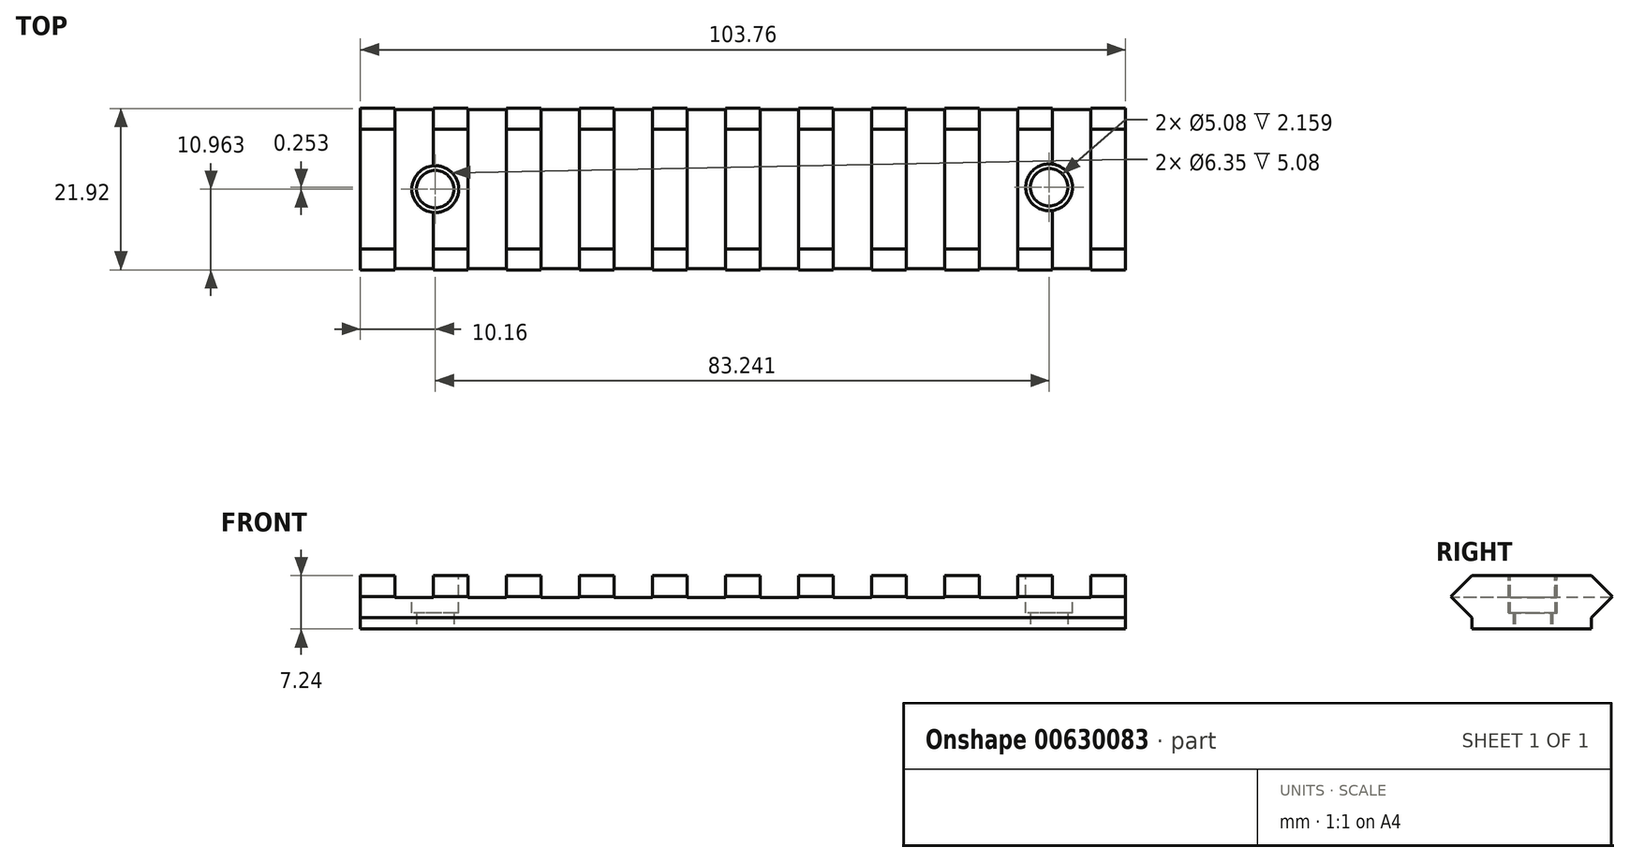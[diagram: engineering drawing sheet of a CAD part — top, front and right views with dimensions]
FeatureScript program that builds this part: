
annotation { "Feature Type Name" : "Feature", "Feature Type Description" : "" }
export const myFeature = defineFeature(function(context is Context, id is Id, definition is map)
    precondition{}
    {
        {
            var Q0;
            Q0=qCreatedBy(makeId("Right.planeOp"),FACE);
            var sketch = newSketch(context, id + "F0", { "sketchPlane" : qUnion([Q0])});
            skLineSegment(sketch, "E0", {"start": v(0, 0) * mm, "end": v(0, 1.52) * mm});
            skLineSegment(sketch, "E1", {"start": v(0, 1.52) * mm, "end": v(-2.86, 4.38) * mm});
            skLineSegment(sketch, "E2", {"start": v(-2.86, 4.38) * mm, "end": v(0, 7.24) * mm});
            skLineSegment(sketch, "E3", {"start": v(0, 7.24) * mm, "end": v(16.2, 7.24) * mm});
            skLineSegment(sketch, "E4", {"start": v(0, 0) * mm, "end": v(16.2, 0) * mm});
            skLineSegment(sketch, "E5", {"start": v(16.2, 0) * mm, "end": v(16.2, 1.52) * mm});
            skLineSegment(sketch, "E6", {"start": v(16.2, 1.52) * mm, "end": v(19.06, 4.38) * mm});
            skLineSegment(sketch, "E7", {"start": v(19.06, 4.38) * mm, "end": v(16.2, 7.24) * mm});
            skSolve(sketch);
        }
        {
            var Q0;
            Q0=makeQuery(id+"F0.imprint","IMPRINT",FACE,{"disambiguationData":[TD([[makeQuery(id+"F0.imprint","IMPRINT",EDGE,{"derivedFrom":sQuery(id+"F0.wireOp",EDGE,"E0")}),-1.0]])]});
            extrude(context, id + "F1", {"entities" : qUnion([Q0]), "depth" : 103.76 * mm});
        }
        {
            var Q0;
            Q0=makeQuery(id+"F1.opExtrude","SWEPT_FACE",FACE,{"disambiguationData":[OSD([sQuery(id+"F0.wireOp",EDGE,"E3")])]});
            var sketch = newSketch(context, id + "F2", { "sketchPlane" : qUnion([Q0])});
            skLineSegment(sketch, "E8", {"start": v(0, 8.1) * mm, "end": v(4.7, 8.1) * mm, "construction": true});
            skLineSegment(sketch, "E9", {"start": v(4.7, 8.1) * mm, "end": v(4.7, 19.06) * mm});
            skLineSegment(sketch, "E10", {"start": v(4.7, 8.1) * mm, "end": v(4.7, -2.86) * mm});
            skLineSegment(sketch, "E11", {"start": v(4.7, 8.1) * mm, "end": v(9.9, 8.1) * mm, "construction": true});
            skLineSegment(sketch, "E12", {"start": v(4.7, 19.06) * mm, "end": v(9.9, 19.06) * mm});
            skLineSegment(sketch, "E13", {"start": v(9.9, 19.06) * mm, "end": v(9.9, -2.86) * mm});
            skLineSegment(sketch, "E14", {"start": v(4.7, -2.86) * mm, "end": v(9.9, -2.86) * mm});
            skLineSegment(sketch, "E15", {"start": v(9.9, 8.1) * mm, "end": v(14.6, 8.1) * mm, "construction": true});
            skLineSegment(sketch, "E16.bottom", {"start": v(14.6, 19.06) * mm, "end": v(19.81, 19.06) * mm});
            skLineSegment(sketch, "E16.top", {"start": v(14.6, -2.86) * mm, "end": v(19.81, -2.86) * mm});
            skLineSegment(sketch, "E16.left", {"start": v(14.6, 19.06) * mm, "end": v(14.6, -2.86) * mm});
            skLineSegment(sketch, "E16.right", {"start": v(19.81, 19.06) * mm, "end": v(19.81, -2.86) * mm});
            skLineSegment(sketch, "E17", {"start": v(19.81, 8.1) * mm, "end": v(24.51, 8.1) * mm, "construction": true});
            skLineSegment(sketch, "E18.bottom", {"start": v(24.51, 19.06) * mm, "end": v(29.72, 19.06) * mm});
            skLineSegment(sketch, "E18.top", {"start": v(24.51, -2.86) * mm, "end": v(29.72, -2.86) * mm});
            skLineSegment(sketch, "E18.left", {"start": v(24.51, 19.06) * mm, "end": v(24.51, -2.86) * mm});
            skLineSegment(sketch, "E18.right", {"start": v(29.72, 19.06) * mm, "end": v(29.72, -2.86) * mm});
            skLineSegment(sketch, "E19.bottom", {"start": v(34.42, 19.06) * mm, "end": v(39.62, 19.06) * mm});
            skLineSegment(sketch, "E19.top", {"start": v(34.42, -2.86) * mm, "end": v(39.62, -2.86) * mm});
            skLineSegment(sketch, "E19.left", {"start": v(34.42, 19.06) * mm, "end": v(34.42, -2.86) * mm});
            skLineSegment(sketch, "E19.right", {"start": v(39.62, 19.06) * mm, "end": v(39.62, -2.86) * mm});
            skLineSegment(sketch, "E20", {"start": v(39.62, 8.1) * mm, "end": v(44.32, 8.1) * mm, "construction": true});
            skLineSegment(sketch, "E21.bottom", {"start": v(44.32, 19.06) * mm, "end": v(49.53, 19.06) * mm});
            skLineSegment(sketch, "E21.top", {"start": v(44.32, -2.86) * mm, "end": v(49.53, -2.86) * mm});
            skLineSegment(sketch, "E21.left", {"start": v(44.32, 19.06) * mm, "end": v(44.32, -2.86) * mm});
            skLineSegment(sketch, "E21.right", {"start": v(49.53, 19.06) * mm, "end": v(49.53, -2.86) * mm});
            skLineSegment(sketch, "E22", {"start": v(49.53, 8.1) * mm, "end": v(54.23, 8.1) * mm, "construction": true});
            skLineSegment(sketch, "E23.bottom", {"start": v(54.23, 19.06) * mm, "end": v(59.44, 19.06) * mm});
            skLineSegment(sketch, "E23.top", {"start": v(54.23, -2.86) * mm, "end": v(59.44, -2.86) * mm});
            skLineSegment(sketch, "E23.left", {"start": v(54.23, 19.06) * mm, "end": v(54.23, -2.86) * mm});
            skLineSegment(sketch, "E23.right", {"start": v(59.44, 19.06) * mm, "end": v(59.44, -2.86) * mm});
            skLineSegment(sketch, "E24", {"start": v(59.44, 8.1) * mm, "end": v(64.13, 8.1) * mm, "construction": true});
            skLineSegment(sketch, "E25.bottom", {"start": v(64.13, 19.06) * mm, "end": v(69.34, 19.06) * mm});
            skLineSegment(sketch, "E25.top", {"start": v(64.13, -2.86) * mm, "end": v(69.34, -2.86) * mm});
            skLineSegment(sketch, "E25.left", {"start": v(64.13, 19.06) * mm, "end": v(64.13, -2.86) * mm});
            skLineSegment(sketch, "E25.right", {"start": v(69.34, 19.06) * mm, "end": v(69.34, -2.86) * mm});
            skLineSegment(sketch, "E26", {"start": v(69.34, 8.1) * mm, "end": v(74.04, 8.1) * mm, "construction": true});
            skLineSegment(sketch, "E27", {"start": v(29.72, 8.1) * mm, "end": v(34.42, 8.1) * mm, "construction": true});
            skLineSegment(sketch, "E28.bottom", {"start": v(74.04, 19.06) * mm, "end": v(79.25, 19.06) * mm});
            skLineSegment(sketch, "E28.top", {"start": v(74.04, -2.86) * mm, "end": v(79.25, -2.86) * mm});
            skLineSegment(sketch, "E28.left", {"start": v(74.04, 19.06) * mm, "end": v(74.04, -2.86) * mm});
            skLineSegment(sketch, "E28.right", {"start": v(79.25, 19.06) * mm, "end": v(79.25, -2.86) * mm});
            skLineSegment(sketch, "E29", {"start": v(79.25, 8.1) * mm, "end": v(83.95, 8.1) * mm, "construction": true});
            skLineSegment(sketch, "E30.bottom", {"start": v(83.95, 19.06) * mm, "end": v(89.15, 19.06) * mm});
            skLineSegment(sketch, "E30.top", {"start": v(83.95, -2.86) * mm, "end": v(89.15, -2.86) * mm});
            skLineSegment(sketch, "E30.left", {"start": v(83.95, 19.06) * mm, "end": v(83.95, -2.86) * mm});
            skLineSegment(sketch, "E30.right", {"start": v(89.15, 19.06) * mm, "end": v(89.15, -2.86) * mm});
            skLineSegment(sketch, "E31", {"start": v(89.15, 8.1) * mm, "end": v(93.85, 8.1) * mm, "construction": true});
            skLineSegment(sketch, "E32.bottom", {"start": v(93.85, 19.15) * mm, "end": v(99.06, 19.15) * mm});
            skLineSegment(sketch, "E32.top", {"start": v(93.85, -2.94) * mm, "end": v(99.06, -2.94) * mm});
            skLineSegment(sketch, "E32.left", {"start": v(93.85, 19.15) * mm, "end": v(93.85, -2.94) * mm});
            skLineSegment(sketch, "E32.right", {"start": v(99.06, 19.15) * mm, "end": v(99.06, -2.94) * mm});
            skSolve(sketch);
        }
        {
            var Q0;
            {var subQ0=sQuery(id+"F2.wireOp",EDGE,"E14");Q0=makeQuery(id+"F2.imprint","IMPRINT",FACE,{"disambiguationData":[TD([[makeQuery(id+"F2.imprint","IMPRINT",EDGE,{"derivedFrom":subQ0}),1.0]])]});}
            var Q1;
            {var subQ0=sQuery(id+"F2.wireOp",EDGE,"E10");var subQ8=sQuery(id+"F2.wireOp",EDGE,"E9");var subQ9=makeQuery(id+"F2.imprint","INTERSECT",VERTEX,{"derivedFrom":[subQ8,subQ0]});Q1=makeQuery(id+"F2.imprint","IMPRINT",FACE,{"disambiguationData":[TD([[makeQuery(id+"F2.imprint","IMPRINT",EDGE,{"disambiguationData":[TD([[subQ9,-1.0]])],"derivedFrom":subQ8}),-1.0]])]});}
            var Q2;
            {var subQ0=sQuery(id+"F2.wireOp",EDGE,"E12");Q2=makeQuery(id+"F2.imprint","IMPRINT",FACE,{"disambiguationData":[TD([[makeQuery(id+"F2.imprint","IMPRINT",EDGE,{"derivedFrom":subQ0}),-1.0]])]});}
            var Q3;
            {var subQ0=sQuery(id+"F2.wireOp",EDGE,"E16.bottom");Q3=makeQuery(id+"F2.imprint","IMPRINT",FACE,{"disambiguationData":[TD([[makeQuery(id+"F2.imprint","IMPRINT",EDGE,{"derivedFrom":subQ0}),-1.0]])]});}
            var Q4;
            {var subQ0=sQuery(id+"F2.wireOp",EDGE,"E16.left");var subQ1=sQuery(id+"F0.wireOp",EDGE,"E3");var subQ2=makeQuery(id+"F1.opExtrude","SWEPT_EDGE",EDGE,{"disambiguationData":[OSD([subQ1,sQuery(id+"F0.wireOp",EDGE,"E7")])]});var subQ3=makeQuery(id+"F2.imprint","INTERSECT",VERTEX,{"derivedFrom":[subQ2,subQ0]});Q4=makeQuery(id+"F2.imprint","IMPRINT",FACE,{"disambiguationData":[TD([[makeQuery(id+"F2.imprint","IMPRINT",EDGE,{"disambiguationData":[TD([[subQ3,-1.0]])],"derivedFrom":subQ0}),1.0]])]});}
            var Q5;
            {var subQ0=sQuery(id+"F2.wireOp",EDGE,"E16.top");Q5=makeQuery(id+"F2.imprint","IMPRINT",FACE,{"disambiguationData":[TD([[makeQuery(id+"F2.imprint","IMPRINT",EDGE,{"derivedFrom":subQ0}),1.0]])]});}
            var Q6;
            {var subQ0=sQuery(id+"F2.wireOp",EDGE,"E18.bottom");Q6=makeQuery(id+"F2.imprint","IMPRINT",FACE,{"disambiguationData":[TD([[makeQuery(id+"F2.imprint","IMPRINT",EDGE,{"derivedFrom":subQ0}),-1.0]])]});}
            var Q7;
            {var subQ0=sQuery(id+"F2.wireOp",EDGE,"E18.left");var subQ1=sQuery(id+"F0.wireOp",EDGE,"E3");var subQ2=makeQuery(id+"F1.opExtrude","SWEPT_EDGE",EDGE,{"disambiguationData":[OSD([subQ1,sQuery(id+"F0.wireOp",EDGE,"E7")])]});var subQ3=makeQuery(id+"F2.imprint","INTERSECT",VERTEX,{"derivedFrom":[subQ2,subQ0]});Q7=makeQuery(id+"F2.imprint","IMPRINT",FACE,{"disambiguationData":[TD([[makeQuery(id+"F2.imprint","IMPRINT",EDGE,{"disambiguationData":[TD([[subQ3,-1.0]])],"derivedFrom":subQ0}),1.0]])]});}
            var Q8;
            {var subQ0=sQuery(id+"F2.wireOp",EDGE,"E18.top");Q8=makeQuery(id+"F2.imprint","IMPRINT",FACE,{"disambiguationData":[TD([[makeQuery(id+"F2.imprint","IMPRINT",EDGE,{"derivedFrom":subQ0}),1.0]])]});}
            var Q9;
            {var subQ0=sQuery(id+"F2.wireOp",EDGE,"E19.bottom");Q9=makeQuery(id+"F2.imprint","IMPRINT",FACE,{"disambiguationData":[TD([[makeQuery(id+"F2.imprint","IMPRINT",EDGE,{"derivedFrom":subQ0}),-1.0]])]});}
            var Q10;
            {var subQ0=sQuery(id+"F2.wireOp",EDGE,"E19.left");var subQ1=sQuery(id+"F0.wireOp",EDGE,"E3");var subQ2=makeQuery(id+"F1.opExtrude","SWEPT_EDGE",EDGE,{"disambiguationData":[OSD([subQ1,sQuery(id+"F0.wireOp",EDGE,"E7")])]});var subQ3=makeQuery(id+"F2.imprint","INTERSECT",VERTEX,{"derivedFrom":[subQ2,subQ0]});Q10=makeQuery(id+"F2.imprint","IMPRINT",FACE,{"disambiguationData":[TD([[makeQuery(id+"F2.imprint","IMPRINT",EDGE,{"disambiguationData":[TD([[subQ3,-1.0]])],"derivedFrom":subQ0}),1.0]])]});}
            var Q11;
            {var subQ0=sQuery(id+"F2.wireOp",EDGE,"E19.top");Q11=makeQuery(id+"F2.imprint","IMPRINT",FACE,{"disambiguationData":[TD([[makeQuery(id+"F2.imprint","IMPRINT",EDGE,{"derivedFrom":subQ0}),1.0]])]});}
            var Q12;
            {var subQ0=sQuery(id+"F2.wireOp",EDGE,"E21.bottom");Q12=makeQuery(id+"F2.imprint","IMPRINT",FACE,{"disambiguationData":[TD([[makeQuery(id+"F2.imprint","IMPRINT",EDGE,{"derivedFrom":subQ0}),-1.0]])]});}
            var Q13;
            {var subQ0=sQuery(id+"F2.wireOp",EDGE,"E21.left");var subQ1=sQuery(id+"F0.wireOp",EDGE,"E3");var subQ2=makeQuery(id+"F1.opExtrude","SWEPT_EDGE",EDGE,{"disambiguationData":[OSD([subQ1,sQuery(id+"F0.wireOp",EDGE,"E7")])]});var subQ3=makeQuery(id+"F2.imprint","INTERSECT",VERTEX,{"derivedFrom":[subQ2,subQ0]});Q13=makeQuery(id+"F2.imprint","IMPRINT",FACE,{"disambiguationData":[TD([[makeQuery(id+"F2.imprint","IMPRINT",EDGE,{"disambiguationData":[TD([[subQ3,-1.0]])],"derivedFrom":subQ0}),1.0]])]});}
            var Q14;
            {var subQ0=sQuery(id+"F2.wireOp",EDGE,"E21.top");Q14=makeQuery(id+"F2.imprint","IMPRINT",FACE,{"disambiguationData":[TD([[makeQuery(id+"F2.imprint","IMPRINT",EDGE,{"derivedFrom":subQ0}),1.0]])]});}
            var Q15;
            {var subQ0=sQuery(id+"F2.wireOp",EDGE,"E23.bottom");Q15=makeQuery(id+"F2.imprint","IMPRINT",FACE,{"disambiguationData":[TD([[makeQuery(id+"F2.imprint","IMPRINT",EDGE,{"derivedFrom":subQ0}),-1.0]])]});}
            var Q16;
            {var subQ0=sQuery(id+"F2.wireOp",EDGE,"E23.left");var subQ1=sQuery(id+"F0.wireOp",EDGE,"E3");var subQ2=makeQuery(id+"F1.opExtrude","SWEPT_EDGE",EDGE,{"disambiguationData":[OSD([subQ1,sQuery(id+"F0.wireOp",EDGE,"E7")])]});var subQ3=makeQuery(id+"F2.imprint","INTERSECT",VERTEX,{"derivedFrom":[subQ2,subQ0]});Q16=makeQuery(id+"F2.imprint","IMPRINT",FACE,{"disambiguationData":[TD([[makeQuery(id+"F2.imprint","IMPRINT",EDGE,{"disambiguationData":[TD([[subQ3,-1.0]])],"derivedFrom":subQ0}),1.0]])]});}
            var Q17;
            {var subQ0=sQuery(id+"F2.wireOp",EDGE,"E23.top");Q17=makeQuery(id+"F2.imprint","IMPRINT",FACE,{"disambiguationData":[TD([[makeQuery(id+"F2.imprint","IMPRINT",EDGE,{"derivedFrom":subQ0}),1.0]])]});}
            var Q18;
            {var subQ0=sQuery(id+"F2.wireOp",EDGE,"E25.bottom");Q18=makeQuery(id+"F2.imprint","IMPRINT",FACE,{"disambiguationData":[TD([[makeQuery(id+"F2.imprint","IMPRINT",EDGE,{"derivedFrom":subQ0}),-1.0]])]});}
            var Q19;
            {var subQ0=sQuery(id+"F2.wireOp",EDGE,"E25.left");var subQ1=sQuery(id+"F0.wireOp",EDGE,"E3");var subQ2=makeQuery(id+"F1.opExtrude","SWEPT_EDGE",EDGE,{"disambiguationData":[OSD([subQ1,sQuery(id+"F0.wireOp",EDGE,"E7")])]});var subQ3=makeQuery(id+"F2.imprint","INTERSECT",VERTEX,{"derivedFrom":[subQ2,subQ0]});Q19=makeQuery(id+"F2.imprint","IMPRINT",FACE,{"disambiguationData":[TD([[makeQuery(id+"F2.imprint","IMPRINT",EDGE,{"disambiguationData":[TD([[subQ3,-1.0]])],"derivedFrom":subQ0}),1.0]])]});}
            var Q20;
            {var subQ0=sQuery(id+"F2.wireOp",EDGE,"E25.top");Q20=makeQuery(id+"F2.imprint","IMPRINT",FACE,{"disambiguationData":[TD([[makeQuery(id+"F2.imprint","IMPRINT",EDGE,{"derivedFrom":subQ0}),1.0]])]});}
            var Q21;
            {var subQ0=sQuery(id+"F2.wireOp",EDGE,"E28.bottom");Q21=makeQuery(id+"F2.imprint","IMPRINT",FACE,{"disambiguationData":[TD([[makeQuery(id+"F2.imprint","IMPRINT",EDGE,{"derivedFrom":subQ0}),-1.0]])]});}
            var Q22;
            {var subQ0=sQuery(id+"F2.wireOp",EDGE,"E28.left");var subQ1=sQuery(id+"F0.wireOp",EDGE,"E3");var subQ2=makeQuery(id+"F1.opExtrude","SWEPT_EDGE",EDGE,{"disambiguationData":[OSD([subQ1,sQuery(id+"F0.wireOp",EDGE,"E7")])]});var subQ3=makeQuery(id+"F2.imprint","INTERSECT",VERTEX,{"derivedFrom":[subQ2,subQ0]});Q22=makeQuery(id+"F2.imprint","IMPRINT",FACE,{"disambiguationData":[TD([[makeQuery(id+"F2.imprint","IMPRINT",EDGE,{"disambiguationData":[TD([[subQ3,-1.0]])],"derivedFrom":subQ0}),1.0]])]});}
            var Q23;
            {var subQ0=sQuery(id+"F2.wireOp",EDGE,"E28.top");Q23=makeQuery(id+"F2.imprint","IMPRINT",FACE,{"disambiguationData":[TD([[makeQuery(id+"F2.imprint","IMPRINT",EDGE,{"derivedFrom":subQ0}),1.0]])]});}
            var Q24;
            {var subQ0=sQuery(id+"F2.wireOp",EDGE,"E30.top");Q24=makeQuery(id+"F2.imprint","IMPRINT",FACE,{"disambiguationData":[TD([[makeQuery(id+"F2.imprint","IMPRINT",EDGE,{"derivedFrom":subQ0}),1.0]])]});}
            var Q25;
            {var subQ0=sQuery(id+"F2.wireOp",EDGE,"E30.left");var subQ1=sQuery(id+"F0.wireOp",EDGE,"E3");var subQ2=makeQuery(id+"F1.opExtrude","SWEPT_EDGE",EDGE,{"disambiguationData":[OSD([subQ1,sQuery(id+"F0.wireOp",EDGE,"E7")])]});var subQ3=makeQuery(id+"F2.imprint","INTERSECT",VERTEX,{"derivedFrom":[subQ2,subQ0]});Q25=makeQuery(id+"F2.imprint","IMPRINT",FACE,{"disambiguationData":[TD([[makeQuery(id+"F2.imprint","IMPRINT",EDGE,{"disambiguationData":[TD([[subQ3,-1.0]])],"derivedFrom":subQ0}),1.0]])]});}
            var Q26;
            {var subQ0=sQuery(id+"F2.wireOp",EDGE,"E30.bottom");Q26=makeQuery(id+"F2.imprint","IMPRINT",FACE,{"disambiguationData":[TD([[makeQuery(id+"F2.imprint","IMPRINT",EDGE,{"derivedFrom":subQ0}),-1.0]])]});}
            var Q27;
            {var subQ0=sQuery(id+"F2.wireOp",EDGE,"E32.bottom");Q27=makeQuery(id+"F2.imprint","IMPRINT",FACE,{"disambiguationData":[TD([[makeQuery(id+"F2.imprint","IMPRINT",EDGE,{"derivedFrom":subQ0}),-1.0]])]});}
            var Q28;
            {var subQ0=sQuery(id+"F2.wireOp",EDGE,"E32.left");var subQ1=sQuery(id+"F0.wireOp",EDGE,"E3");var subQ2=makeQuery(id+"F1.opExtrude","SWEPT_EDGE",EDGE,{"disambiguationData":[OSD([subQ1,sQuery(id+"F0.wireOp",EDGE,"E7")])]});var subQ3=makeQuery(id+"F2.imprint","INTERSECT",VERTEX,{"derivedFrom":[subQ2,subQ0]});Q28=makeQuery(id+"F2.imprint","IMPRINT",FACE,{"disambiguationData":[TD([[makeQuery(id+"F2.imprint","IMPRINT",EDGE,{"disambiguationData":[TD([[subQ3,-1.0]])],"derivedFrom":subQ0}),1.0]])]});}
            var Q29;
            {var subQ0=sQuery(id+"F2.wireOp",EDGE,"E32.top");Q29=makeQuery(id+"F2.imprint","IMPRINT",FACE,{"disambiguationData":[TD([[makeQuery(id+"F2.imprint","IMPRINT",EDGE,{"derivedFrom":subQ0}),1.0]])]});}
            extrude(context, id + "F3", {"entities" : qUnion([Q0, Q1, Q2, Q3, Q4, Q5, Q6, Q7, Q8, Q9, Q10, Q11, Q12, Q13, Q14, Q15, Q16, Q17, Q18, Q19, Q20, Q21, Q22, Q23, Q24, Q25, Q26, Q27, Q28, Q29]), "operationType" : NewBodyOperationType.REMOVE, "oppositeDirection" : true, "depth" : 3 * mm});
        }
        {
            var Q0;
            Q0=makeQuery(id+"F1.opExtrude","SWEPT_FACE",FACE,{"disambiguationData":[OSD([sQuery(id+"F0.wireOp",EDGE,"E4")])]});
            var sketch = newSketch(context, id + "F4", { "sketchPlane" : qUnion([Q0])});
            skCircle(sketch, "E33", {"center": v(93.4, -8.36) * mm, "radius": 2.54 * mm});
            skCircle(sketch, "E34", {"center": v(10.16, -8.1) * mm, "radius": 2.54 * mm});
            skLineSegment(sketch, "E35", {"start": v(10.16, -8.1) * mm, "end": v(0, -8.1) * mm, "construction": true});
            skPoint(sketch, "E35.endSnap0", {"position": v(0, -8.1) * mm});
            skLineSegment(sketch, "E36", {"start": v(93.4, -8.36) * mm, "end": v(10.16, -8.1) * mm, "construction": true});
            skSolve(sketch);
        }
        {
            var Q0;
            Q0=makeQuery(id+"F4.imprint","IMPRINT",FACE,{"disambiguationData":[TD([[makeQuery(id+"F4.imprint","IMPRINT",EDGE,{"derivedFrom":sQuery(id+"F4.wireOp",EDGE,"E33")}),1.0]])]});
            var Q1;
            Q1=makeQuery(id+"F4.imprint","IMPRINT",FACE,{"disambiguationData":[TD([[makeQuery(id+"F4.imprint","IMPRINT",EDGE,{"derivedFrom":sQuery(id+"F4.wireOp",EDGE,"E34")}),1.0]])]});
            extrude(context, id + "F5", {"entities" : qUnion([Q0, Q1]), "operationType" : NewBodyOperationType.REMOVE, "oppositeDirection" : true, "depth" : 7.24 * mm, "offsetDistance" : 25 * mm});
        }
        {
            var Q0;
            Q0=makeQuery(id+"F3.boolean.opBoolean","SPLIT",FACE,{"disambiguationData":[TD([makeQuery(id+"F3.opExtrude","SWEPT_FACE",FACE,{"disambiguationData":[OSD([sQuery(id+"F2.wireOp",EDGE,"E18.right")])]})])],"derivedFrom":makeQuery(id+"F1.opExtrude","SWEPT_FACE",FACE,{"disambiguationData":[OSD([sQuery(id+"F0.wireOp",EDGE,"E3")])]})});
            var sketch = newSketch(context, id + "F6", { "sketchPlane" : qUnion([Q0])});
            skCircle(sketch, "E37", {"center": v(10.16, 8.1) * mm, "radius": 3.18 * mm});
            skCircle(sketch, "E38", {"center": v(93.4, 8.36) * mm, "radius": 3.18 * mm});
            skCircle(sketch, "E39", {"center": v(10.16, 8.1) * mm, "radius": 2.54 * mm, "construction": true});
            skCircle(sketch, "E40", {"center": v(93.4, 8.36) * mm, "radius": 2.54 * mm, "construction": true});
            skSolve(sketch);
        }
        {
            var Q0;
            Q0=makeQuery(id+"F6.imprint","IMPRINT",FACE,{"disambiguationData":[TD([[makeQuery(id+"F6.imprint","IMPRINT",EDGE,{"derivedFrom":sQuery(id+"F6.wireOp",EDGE,"E38")}),1.0]])]});
            var Q1;
            Q1=makeQuery(id+"F6.imprint","IMPRINT",FACE,{"disambiguationData":[TD([[makeQuery(id+"F6.imprint","IMPRINT",EDGE,{"derivedFrom":sQuery(id+"F6.wireOp",EDGE,"E37")}),1.0]])]});
            extrude(context, id + "F7", {"entities" : qUnion([Q0, Q1]), "operationType" : NewBodyOperationType.REMOVE, "oppositeDirection" : true, "depth" : 5.08 * mm});
        }
    });
